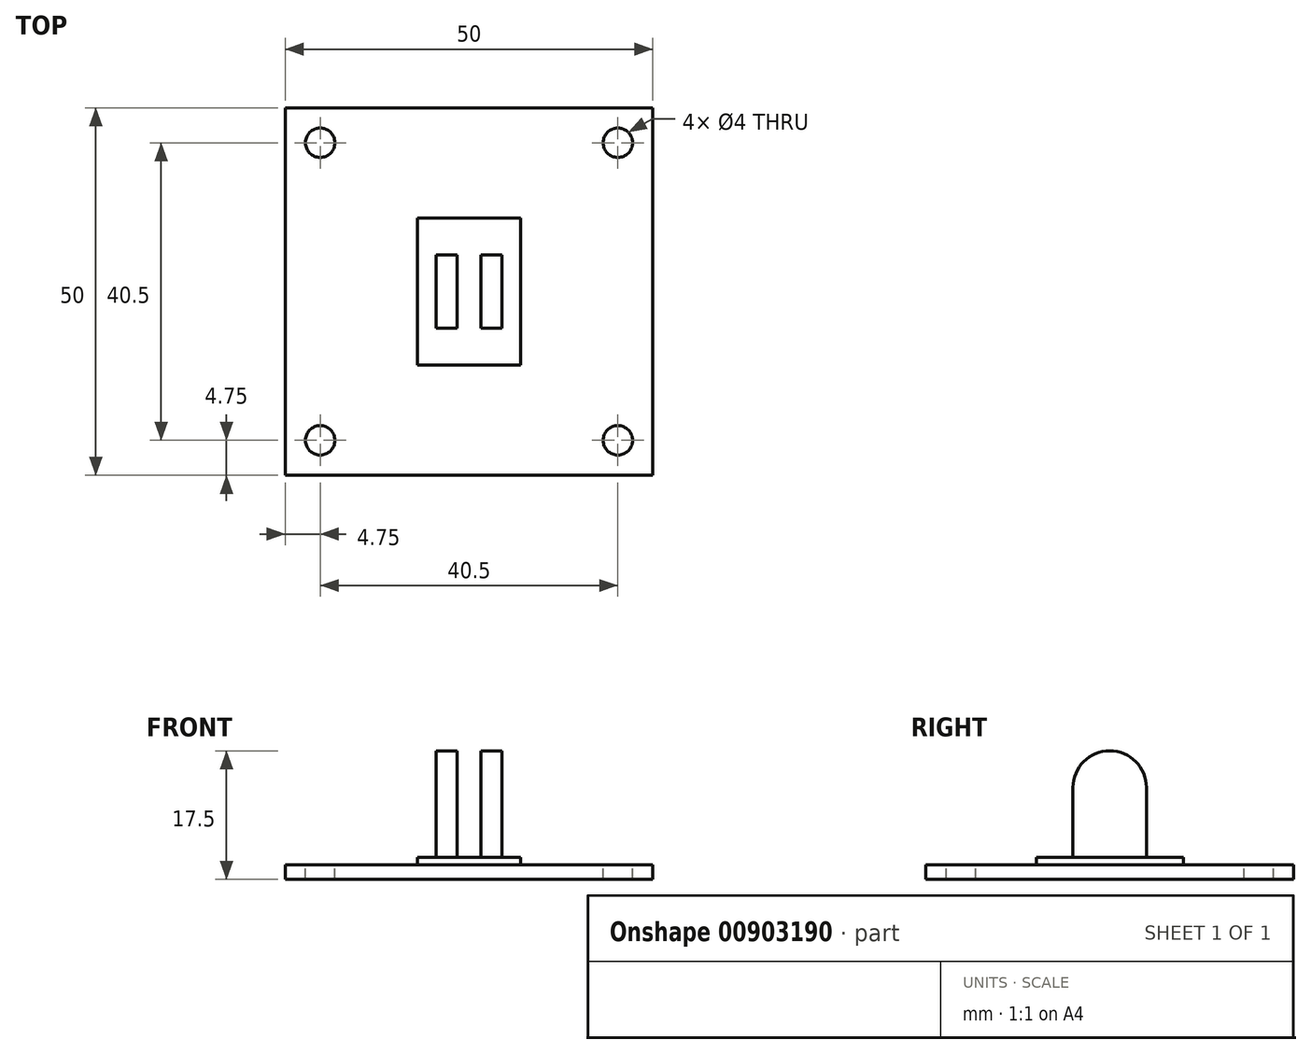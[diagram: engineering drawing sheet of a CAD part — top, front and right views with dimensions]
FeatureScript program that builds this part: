
annotation { "Feature Type Name" : "Feature", "Feature Type Description" : "" }
export const myFeature = defineFeature(function(context is Context, id is Id, definition is map)
    precondition{}
    {
        {
            var Q0;
            Q0=qCreatedBy(makeId("Top.planeOp"),FACE);
            var sketch = newSketch(context, id + "F0", { "sketchPlane" : qUnion([Q0])});
            skLineSegment(sketch, "E0.bottom", {"start": v(25, -25) * mm, "end": v(-25, -25) * mm});
            skLineSegment(sketch, "E0.top", {"start": v(25, 25) * mm, "end": v(-25, 25) * mm});
            skLineSegment(sketch, "E0.left", {"start": v(25, -25) * mm, "end": v(25, 25) * mm});
            skLineSegment(sketch, "E0.right", {"start": v(-25, -25) * mm, "end": v(-25, 25) * mm});
            skPoint(sketch, "E0.middle", {"position": v(0, 0) * mm});
            skSolve(sketch);
        }
        {
            var Q0;
            Q0 = qSketchRegion(id + "F0", true);
            extrude(context, id + "F1", {"entities" : qUnion([Q0]), "depth" : 2 * mm, "offsetDistance" : 25 * mm});
        }
        {
            var Q0;
            Q0=makeQuery(id+"F1.opExtrude","CAP_FACE",FACE,{"disambiguationData":[OSD([sQuery(id+"F0.wireOp",EDGE,"E0.bottom"),sQuery(id+"F0.wireOp",EDGE,"E0.top"),sQuery(id+"F0.wireOp",EDGE,"E0.left"),sQuery(id+"F0.wireOp",EDGE,"E0.right")])],"isStart":false});
            var sketch = newSketch(context, id + "F2", { "sketchPlane" : qUnion([Q0])});
            skCircle(sketch, "E1", {"center": v(-20.25, 20.25) * mm, "radius": 2 * mm});
            skCircle(sketch, "E2", {"center": v(20.25, 20.25) * mm, "radius": 2 * mm});
            skCircle(sketch, "E3", {"center": v(20.25, -20.25) * mm, "radius": 2 * mm});
            skCircle(sketch, "E4", {"center": v(-20.25, -20.25) * mm, "radius": 2 * mm});
            skSolve(sketch);
        }
        {
            var Q0;
            Q0 = qSketchRegion(id + "F2", true);
            extrude(context, id + "F3", {"entities" : qUnion([Q0]), "operationType" : NewBodyOperationType.REMOVE, "oppositeDirection" : true, "depth" : 2 * mm, "offsetDistance" : 25 * mm});
        }
        {
            var Q0;
            Q0=makeQuery(id+"F2.imprint","IMPRINT",FACE,{"disambiguationData":[TD([[makeQuery(id+"F2.imprint","IMPRINT",EDGE,{"derivedFrom":sQuery(id+"F2.wireOp",EDGE,"E1")}),-1.0]])]});
            var sketch = newSketch(context, id + "F4", { "sketchPlane" : qUnion([Q0])});
            skLineSegment(sketch, "E5.bottom", {"start": v(7, -10) * mm, "end": v(-7, -10) * mm});
            skLineSegment(sketch, "E5.top", {"start": v(7, 10) * mm, "end": v(-7, 10) * mm});
            skLineSegment(sketch, "E5.left", {"start": v(7, -10) * mm, "end": v(7, 10) * mm});
            skLineSegment(sketch, "E5.right", {"start": v(-7, -10) * mm, "end": v(-7, 10) * mm});
            skPoint(sketch, "E5.middle", {"position": v(0, 0) * mm});
            skSolve(sketch);
        }
        {
            var Q0;
            Q0 = qSketchRegion(id + "F4", true);
            extrude(context, id + "F5", {"entities" : qUnion([Q0]), "operationType" : NewBodyOperationType.ADD, "depth" : 1 * mm, "offsetDistance" : 25 * mm});
        }
        {
            var Q0;
            Q0=makeQuery(id+"F5.opExtrude","CAP_FACE",FACE,{"disambiguationData":[OSD([sQuery(id+"F4.wireOp",EDGE,"E5.bottom"),sQuery(id+"F4.wireOp",EDGE,"E5.top"),sQuery(id+"F4.wireOp",EDGE,"E5.left"),sQuery(id+"F4.wireOp",EDGE,"E5.right")])],"isStart":false});
            var sketch = newSketch(context, id + "F6", { "sketchPlane" : qUnion([Q0])});
            skLineSegment(sketch, "E6.left", {"start": v(1.6, 0) * mm, "end": v(1.6, 0) * mm});
            skLineSegment(sketch, "E6.right", {"start": v(-1.6, 5) * mm, "end": v(-1.6, 5) * mm});
            skPoint(sketch, "E6.middle", {"position": v(0, 0) * mm});
            skLineSegment(sketch, "E7.bottom", {"start": v(1.6, 5) * mm, "end": v(4.5, 5) * mm});
            skLineSegment(sketch, "E7.top", {"start": v(1.6, -5) * mm, "end": v(4.5, -5) * mm});
            skLineSegment(sketch, "E7.left", {"start": v(1.6, 5) * mm, "end": v(1.6, -5) * mm});
            skLineSegment(sketch, "E7.right", {"start": v(4.5, 5) * mm, "end": v(4.5, -5) * mm});
            skLineSegment(sketch, "E8.bottom", {"start": v(-1.6, 5) * mm, "end": v(-4.5, 5) * mm});
            skLineSegment(sketch, "E8.top", {"start": v(-1.6, -5) * mm, "end": v(-4.5, -5) * mm});
            skLineSegment(sketch, "E8.left", {"start": v(-1.6, 5) * mm, "end": v(-1.6, -5) * mm});
            skLineSegment(sketch, "E8.right", {"start": v(-4.5, 5) * mm, "end": v(-4.5, -5) * mm});
            skSolve(sketch);
        }
        {
            var Q0;
            Q0 = qSketchRegion(id + "F6", true);
            extrude(context, id + "F7", {"entities" : qUnion([Q0]), "operationType" : NewBodyOperationType.ADD, "depth" : 14.5 * mm, "offsetDistance" : 25 * mm});
        }
        {
            var Q0;
            Q0=makeQuery(id+"F7.opExtrude","CAP_EDGE",EDGE,{"disambiguationData":[OSD([sQuery(id+"F6.wireOp",EDGE,"E8.bottom")])],"isStart":false});
            var Q1;
            Q1=makeQuery(id+"F7.opExtrude","CAP_EDGE",EDGE,{"disambiguationData":[OSD([sQuery(id+"F6.wireOp",EDGE,"E7.bottom")])],"isStart":false});
            var Q2;
            Q2=makeQuery(id+"F7.opExtrude","CAP_EDGE",EDGE,{"disambiguationData":[OSD([sQuery(id+"F6.wireOp",EDGE,"E7.top")])],"isStart":false});
            var Q3;
            Q3=makeQuery(id+"F7.opExtrude","CAP_EDGE",EDGE,{"disambiguationData":[OSD([sQuery(id+"F6.wireOp",EDGE,"E8.top")])],"isStart":false});
            fillet(context, id + "F8", {"entities" : qUnion([Q0, Q1, Q2, Q3]), "radius" : 5 * mm, "tangentPropagation" : true, "allowEdgeOverflow" : false});
        }
    });
